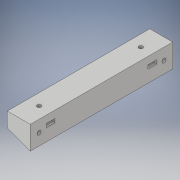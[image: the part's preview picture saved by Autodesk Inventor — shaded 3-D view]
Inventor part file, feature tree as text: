
AUTODESK INVENTOR PART (.ipt)
format: ipt  version: 2019 (Build 230136000, 136)  size: 136,704 bytes
history: native  units: mm
features: extrude x4, sketch x4, other x2, projected_geometry x2
ambient origin geometry x8: Origin, YZ Plane, XZ Plane, XY Plane, X Axis, Y Axis, Z Axis, Center Point
bodies: Body1 (feature_tree)
feature tree (12):
  other  "Твердое тело1"
  extrude  "Выдавливание1"  Depth=10.0mm
  extrude  "Выдавливание2"  Depth=15.8mm
  other  "РабПлоскость1"
  extrude  "Выдавливание3"  Depth=16.0mm
  extrude  "Выдавливание4"  Depth=98.0mm TaperAngle=0.0deg
  sketch  "Эскиз1"
  sketch  "Эскиз2"
  sketch  "Эскиз4"
  sketch  "Эскиз5"
  projected_geometry  "Спроецированная петля1"
  projected_geometry  "Спроецированная петля2"
